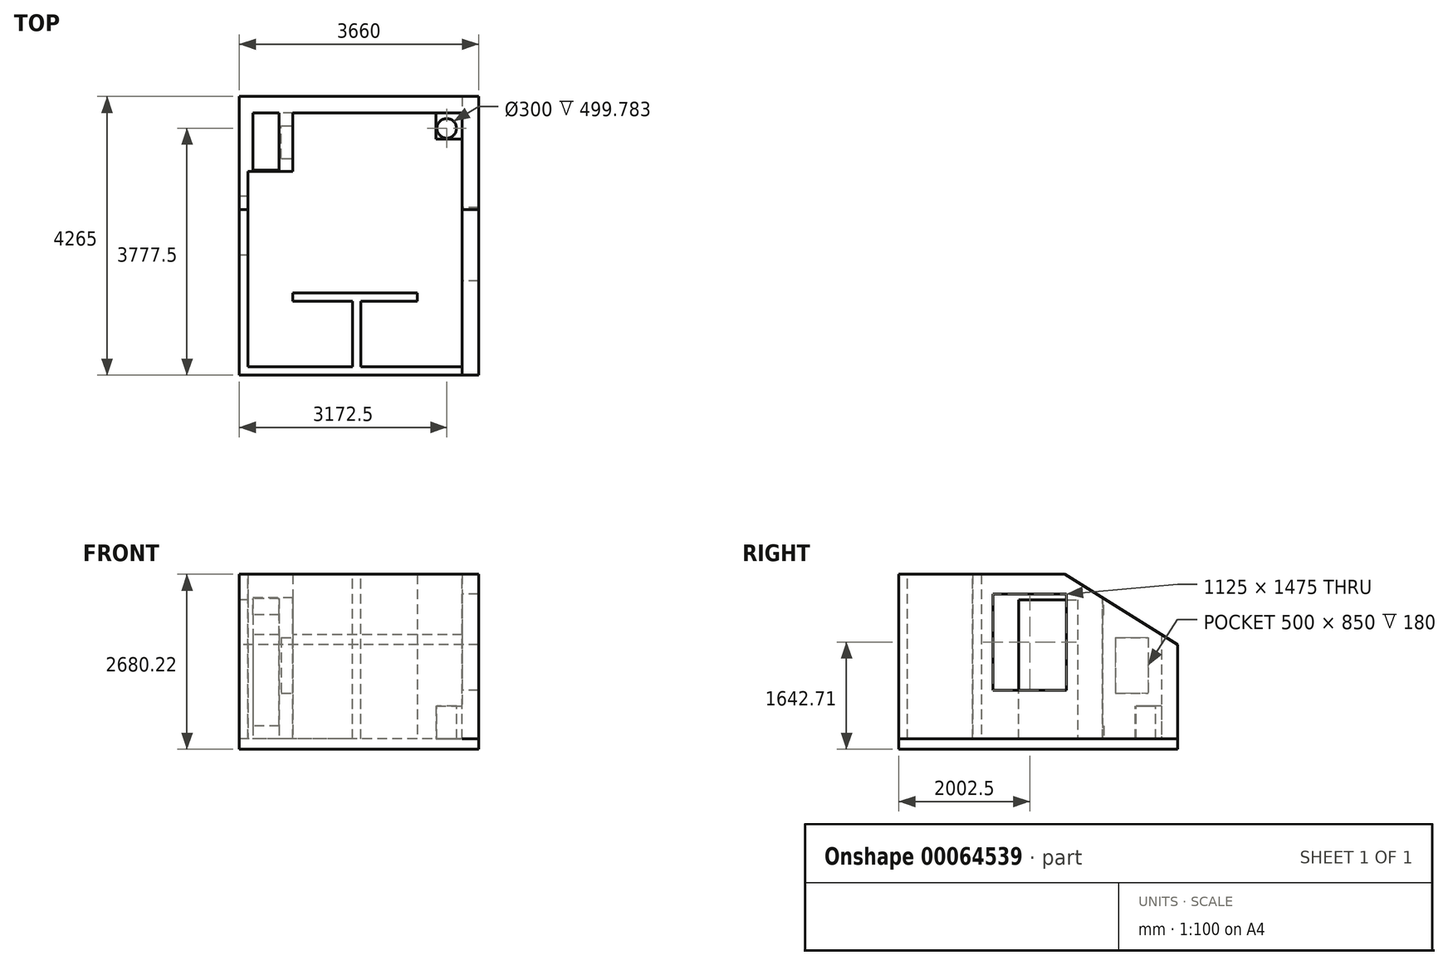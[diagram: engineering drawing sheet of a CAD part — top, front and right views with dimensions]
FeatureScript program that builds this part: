
annotation { "Feature Type Name" : "Feature", "Feature Type Description" : "" }
export const myFeature = defineFeature(function(context is Context, id is Id, definition is map)
    precondition{}
    {
        {
            var Q0;
            Q0=qCreatedBy(makeId("Right.planeOp"),FACE);
            var sketch = newSketch(context, id + "F0", { "sketchPlane" : qUnion([Q0])});
            skLineSegment(sketch, "E0", {"start": v(-1232.64, -1486.91) * mm, "end": v(-1232.64, 1033.09) * mm});
            skLineSegment(sketch, "E1", {"start": v(-1232.64, 1033.09) * mm, "end": v(1304, 1033.09) * mm});
            skLineSegment(sketch, "E2", {"start": v(1304, 1033.09) * mm, "end": v(2782.36, 109.3) * mm});
            skLineSegment(sketch, "E3", {"start": v(2782.36, 109.3) * mm, "end": v(2782.36, -1486.91) * mm});
            skLineSegment(sketch, "E4", {"start": v(2782.36, -1486.91) * mm, "end": v(-1232.64, -1486.91) * mm});
            skLineSegment(sketch, "E5", {"start": v(602.36, -1486.91) * mm, "end": v(602.36, 643.09) * mm});
            skLineSegment(sketch, "E6", {"start": v(602.36, 643.09) * mm, "end": v(1502.36, 643.09) * mm});
            skLineSegment(sketch, "E7", {"start": v(1502.36, 643.09) * mm, "end": v(1502.36, -1486.91) * mm});
            skLineSegment(sketch, "E8", {"start": v(1882.36, 671.69) * mm, "end": v(1882.36, -1486.91) * mm});
            skLineSegment(sketch, "E9", {"start": v(2782.36, -1486.91) * mm, "end": v(3032.36, -1486.91) * mm});
            skLineSegment(sketch, "E10", {"start": v(3032.36, -1486.91) * mm, "end": v(3032.36, -46.91) * mm});
            skLineSegment(sketch, "E11", {"start": v(3032.36, -46.91) * mm, "end": v(2782.36, 109.3) * mm});
            skSolve(sketch);
        }
        {
            var Q0;
            {var subQ6=sQuery(id+"F0.wireOp",EDGE,"E0");Q0=makeQuery(id+"F0.imprint","IMPRINT",FACE,{"disambiguationData":[TD([[makeQuery(id+"F0.imprint","IMPRINT",EDGE,{"derivedFrom":subQ6}),-1.0]])]});}
            extrude(context, id + "F1", {"entities" : qUnion([Q0]), "depth" : 130 * mm});
        }
        {
            var Q0;
            {var subQ0=sQuery(id+"F0.wireOp",EDGE,"E3");Q0=makeQuery(id+"F0.imprint","IMPRINT",FACE,{"disambiguationData":[TD([[makeQuery(id+"F0.imprint","IMPRINT",EDGE,{"derivedFrom":subQ0}),-1.0]])]});}
            extrude(context, id + "F2", {"entities" : qUnion([Q0]), "operationType" : NewBodyOperationType.ADD, "depth" : 210 * mm});
        }
        {
            var Q0;
            Q0=makeQuery(id+"F0.imprint","IMPRINT",FACE,{"disambiguationData":[TD([[makeQuery(id+"F0.imprint","IMPRINT",EDGE,{"derivedFrom":sQuery(id+"F0.wireOp",EDGE,"E3")}),1.0]])]});
            extrude(context, id + "F3", {"entities" : qUnion([Q0]), "operationType" : NewBodyOperationType.ADD, "depth" : 3280 * mm + 130 * mm});
        }
        {
            var Q0;
            Q0=makeQuery(id+"F3.opExtrude","CAP_FACE",FACE,{"disambiguationData":[OSD([sQuery(id+"F0.wireOp",EDGE,"E3"),sQuery(id+"F0.wireOp",EDGE,"E9"),sQuery(id+"F0.wireOp",EDGE,"E10"),sQuery(id+"F0.wireOp",EDGE,"E11")])],"isStart":false});
            var sketch = newSketch(context, id + "F4", { "sketchPlane" : qUnion([Q0])});
            skLineSegment(sketch, "E12", {"start": v(-1232.64, -1486.7) * mm, "end": v(-1232.64, 1033.3) * mm});
            skLineSegment(sketch, "E13", {"start": v(-1232.64, 1033.3) * mm, "end": v(1303.65, 1033.3) * mm});
            skLineSegment(sketch, "E14", {"start": v(1303.65, 1033.3) * mm, "end": v(2782.36, 109.3) * mm});
            skLineSegment(sketch, "E15", {"start": v(2782.36, 109.3) * mm, "end": v(2782.36, -1486.7) * mm});
            skLineSegment(sketch, "E16", {"start": v(2782.36, -1486.7) * mm, "end": v(-1232.64, -1486.7) * mm});
            skLineSegment(sketch, "E17", {"start": v(1882.36, 671.69) * mm, "end": v(1882.36, -1486.7) * mm});
            skLineSegment(sketch, "E18", {"start": v(2782.36, -1486.7) * mm, "end": v(3032.36, -1486.7) * mm});
            skLineSegment(sketch, "E19", {"start": v(3032.36, -1486.7) * mm, "end": v(3032.36, -46.91) * mm});
            skLineSegment(sketch, "E20", {"start": v(3032.36, -46.91) * mm, "end": v(2782.36, 109.3) * mm});
            skLineSegment(sketch, "E21.bottom", {"start": v(207.36, 733.3) * mm, "end": v(1332.36, 733.3) * mm});
            skLineSegment(sketch, "E21.top", {"start": v(207.36, -741.7) * mm, "end": v(1332.36, -741.7) * mm});
            skLineSegment(sketch, "E21.left", {"start": v(207.36, 733.3) * mm, "end": v(207.36, -741.7) * mm});
            skLineSegment(sketch, "E21.right", {"start": v(1332.36, 733.3) * mm, "end": v(1332.36, -741.7) * mm});
            skSolve(sketch);
        }
        {
            var Q0;
            Q0 = qSketchRegion(id + "F4", true);
            extrude(context, id + "F5", {"entities" : qUnion([Q0]), "operationType" : NewBodyOperationType.ADD, "depth" : 250 * mm});
        }
        {
            var Q0;
            Q0=makeQuery(id+"F2.opExtrude","CAP_FACE",FACE,{"disambiguationData":[OSD([sQuery(id+"F0.wireOp",EDGE,"E2"),sQuery(id+"F0.wireOp",EDGE,"E3"),sQuery(id+"F0.wireOp",EDGE,"E4"),sQuery(id+"F0.wireOp",EDGE,"E8")])],"isStart":false});
            cPlane(context, id + "F6", {"entities" : qUnion([Q0]), "cplaneType" : CPlaneType.OFFSET, "offset" : 400 * mm, "width" : 150 * mm, "height" : 150 * mm});
        }
        {
            var Q0;
            Q0=qCreatedBy(id+"F6.planeOp",FACE);
            var sketch = newSketch(context, id + "F7", { "sketchPlane" : qUnion([Q0])});
            skLineSegment(sketch, "E22", {"start": v(1882.36, 671.69) * mm, "end": v(2782.36, 109.3) * mm});
            skLineSegment(sketch, "E23", {"start": v(2782.36, 109.3) * mm, "end": v(2782.36, -1486.7) * mm});
            skLineSegment(sketch, "E24", {"start": v(2782.36, -1486.7) * mm, "end": v(2782.36, -1486.7) * mm});
            skLineSegment(sketch, "E25", {"start": v(2782.36, 109.3) * mm, "end": v(2782.36, 109.3) * mm});
            skLineSegment(sketch, "E26", {"start": v(2782.36, -1486.7) * mm, "end": v(1882.36, -1486.7) * mm});
            skLineSegment(sketch, "E27", {"start": v(1882.36, -1486.7) * mm, "end": v(1882.36, 671.69) * mm});
            skSolve(sketch);
        }
        {
            var Q0;
            Q0 = qSketchRegion(id + "F7", true);
            extrude(context, id + "F8", {"entities" : qUnion([Q0]), "depth" : 210 * mm});
        }
        {
            var Q0;
            Q0=makeQuery(id+"F8.opExtrude","CAP_FACE",FACE,{"disambiguationData":[OSD([sQuery(id+"F7.wireOp",EDGE,"E22"),sQuery(id+"F7.wireOp",EDGE,"E23"),sQuery(id+"F7.wireOp",EDGE,"E26"),sQuery(id+"F7.wireOp",EDGE,"E27")])],"isStart":false});
            var sketch = newSketch(context, id + "F9", { "sketchPlane" : qUnion([Q0])});
            skLineSegment(sketch, "E28.bottom", {"start": v(2082.36, 63.3) * mm, "end": v(2582.36, 63.3) * mm});
            skLineSegment(sketch, "E28.top", {"start": v(2082.36, -786.7) * mm, "end": v(2582.36, -786.7) * mm});
            skLineSegment(sketch, "E28.left", {"start": v(2082.36, 63.3) * mm, "end": v(2082.36, -786.7) * mm});
            skLineSegment(sketch, "E28.right", {"start": v(2582.36, 63.3) * mm, "end": v(2582.36, -786.7) * mm});
            skSolve(sketch);
        }
        {
            var Q0;
            Q0=makeQuery(id+"F9.imprint","IMPRINT",FACE,{"disambiguationData":[TD([[makeQuery(id+"F9.imprint","IMPRINT",EDGE,{"derivedFrom":sQuery(id+"F9.wireOp",EDGE,"E28.bottom")}),-1.0]])]});
            extrude(context, id + "F10", {"entities" : qUnion([Q0]), "operationType" : NewBodyOperationType.REMOVE, "oppositeDirection" : true, "depth" : 180 * mm});
        }
        {
            var Q0;
            Q0=makeQuery(id+"F2.opExtrude","CAP_FACE",FACE,{"disambiguationData":[OSD([sQuery(id+"F0.wireOp",EDGE,"E2"),sQuery(id+"F0.wireOp",EDGE,"E3"),sQuery(id+"F0.wireOp",EDGE,"E4"),sQuery(id+"F0.wireOp",EDGE,"E8")])],"isStart":false});
            var sketch = newSketch(context, id + "F11", { "sketchPlane" : qUnion([Q0])});
            skLineSegment(sketch, "E29", {"start": v(1882.36, 671.69) * mm, "end": v(1882.36, 413.09) * mm});
            skLineSegment(sketch, "E30", {"start": v(1882.36, 413.09) * mm, "end": v(1902.36, 413.09) * mm});
            skLineSegment(sketch, "E31", {"start": v(1902.36, 413.09) * mm, "end": v(1902.36, 659.2) * mm});
            skLineSegment(sketch, "E32", {"start": v(1902.36, 659.2) * mm, "end": v(1882.36, 671.69) * mm});
            skLineSegment(sketch, "E33", {"start": v(1882.36, -1486.91) * mm, "end": v(1882.36, -1286.91) * mm});
            skLineSegment(sketch, "E34", {"start": v(1882.36, -1286.91) * mm, "end": v(1902.36, -1286.91) * mm});
            skLineSegment(sketch, "E35", {"start": v(1902.36, -1286.91) * mm, "end": v(1902.36, -1486.91) * mm});
            skLineSegment(sketch, "E36", {"start": v(1902.36, -1486.91) * mm, "end": v(1882.36, -1486.91) * mm});
            skSolve(sketch);
        }
        {
            var Q0;
            Q0=makeQuery(id+"F11.imprint","IMPRINT",FACE,{"disambiguationData":[TD([[makeQuery(id+"F11.imprint","IMPRINT",EDGE,{"derivedFrom":sQuery(id+"F11.wireOp",EDGE,"E33")}),1.0]])]});
            var Q1;
            Q1=makeQuery(id+"F11.imprint","IMPRINT",FACE,{"disambiguationData":[TD([[makeQuery(id+"F11.imprint","IMPRINT",EDGE,{"derivedFrom":sQuery(id+"F11.wireOp",EDGE,"E29")}),1.0]])]});
            extrude(context, id + "F12", {"entities" : qUnion([Q0, Q1]), "operationType" : NewBodyOperationType.ADD, "depth" : 400 * mm});
        }
        {
            var Q0;
            Q0=makeQuery(id+"F5.opExtrude","CAP_FACE",FACE,{"disambiguationData":[OSD([sQuery(id+"F4.wireOp",EDGE,"E12"),sQuery(id+"F4.wireOp",EDGE,"E13"),sQuery(id+"F4.wireOp",EDGE,"E14"),sQuery(id+"F4.wireOp",EDGE,"E16"),sQuery(id+"F4.wireOp",EDGE,"E18"),sQuery(id+"F4.wireOp",EDGE,"E19"),sQuery(id+"F4.wireOp",EDGE,"E20"),sQuery(id+"F4.wireOp",EDGE,"E21.bottom"),sQuery(id+"F4.wireOp",EDGE,"E21.top"),sQuery(id+"F4.wireOp",EDGE,"E21.left"),sQuery(id+"F4.wireOp",EDGE,"E21.right")])],"isStart":true});
            var sketch = newSketch(context, id + "F13", { "sketchPlane" : qUnion([Q0])});
            skLineSegment(sketch, "E37", {"start": v(-2382.36, -1486.91) * mm, "end": v(-2382.36, 359.25) * mm});
            skLineSegment(sketch, "E38", {"start": v(-2382.36, 359.25) * mm, "end": v(-2257.36, 437.36) * mm});
            skLineSegment(sketch, "E39", {"start": v(-2257.36, 437.36) * mm, "end": v(-2257.36, -1486.91) * mm});
            skLineSegment(sketch, "E40", {"start": v(-2257.36, -1486.91) * mm, "end": v(-2382.36, -1486.91) * mm});
            skLineSegment(sketch, "E41.bottom", {"start": v(-2782.36, -1486.91) * mm, "end": v(-2382.36, -1486.91) * mm});
            skLineSegment(sketch, "E41.top", {"start": v(-2782.36, -986.91) * mm, "end": v(-2382.36, -986.91) * mm});
            skLineSegment(sketch, "E41.left", {"start": v(-2782.36, -1486.91) * mm, "end": v(-2782.36, -986.91) * mm});
            skLineSegment(sketch, "E41.right", {"start": v(-2382.36, -1486.91) * mm, "end": v(-2382.36, -986.91) * mm});
            skSolve(sketch);
        }
        {
            var Q0;
            {var subQ5=sQuery(id+"F13.wireOp",EDGE,"E41.left");Q0=makeQuery(id+"F13.imprint","IMPRINT",FACE,{"disambiguationData":[TD([[makeQuery(id+"F13.imprint","IMPRINT",EDGE,{"derivedFrom":subQ5}),1.0]])]});}
            var Q1;
            {var subQ5=sQuery(id+"F13.wireOp",EDGE,"E41.right");Q1=makeQuery(id+"F13.imprint","IMPRINT",FACE,{"disambiguationData":[TD([[makeQuery(id+"F13.imprint","IMPRINT",EDGE,{"derivedFrom":subQ5}),1.0]])]});}
            extrude(context, id + "F14", {"entities" : qUnion([Q0, Q1]), "operationType" : NewBodyOperationType.ADD, "depth" : 400 * mm});
        }
        {
            var Q0;
            Q0=makeQuery(id+"F14.opExtrude","SWEPT_FACE",FACE,{"disambiguationData":[OSD([sQuery(id+"F13.wireOp",EDGE,"E41.top")])]});
            var sketch = newSketch(context, id + "F15", { "sketchPlane" : qUnion([Q0])});
            skCircle(sketch, "E42", {"center": v(3172.5, 2544.86) * mm, "radius": 150 * mm});
            skSolve(sketch);
        }
        {
            var Q0;
            Q0=makeQuery(id+"F15.imprint","IMPRINT",FACE,{"disambiguationData":[TD([[makeQuery(id+"F15.imprint","IMPRINT",EDGE,{"derivedFrom":sQuery(id+"F15.wireOp",EDGE,"E42")}),1.0]])]});
            var Q1;
            Q1=sQuery(id+"F15.wireOp",EDGE,"E42");
            extrude(context, id + "F16", {"entities" : qUnion([Q0]), "operationType" : NewBodyOperationType.REMOVE, "surfaceEntities" : qUnion([Q1]), "endBound" : BoundingType.UP_TO_NEXT, "oppositeDirection" : true, "depth" : 25 * mm});
        }
        {
            var Q0;
            Q0=makeQuery(id+"F1.opExtrude","CAP_FACE",FACE,{"disambiguationData":[OSD([sQuery(id+"F0.wireOp",EDGE,"E0"),sQuery(id+"F0.wireOp",EDGE,"E1"),sQuery(id+"F0.wireOp",EDGE,"E2"),sQuery(id+"F0.wireOp",EDGE,"E4"),sQuery(id+"F0.wireOp",EDGE,"E5"),sQuery(id+"F0.wireOp",EDGE,"E6"),sQuery(id+"F0.wireOp",EDGE,"E7"),sQuery(id+"F0.wireOp",EDGE,"E8")])],"isStart":false});
            var sketch = newSketch(context, id + "F17", { "sketchPlane" : qUnion([Q0])});
            skLineSegment(sketch, "E43.bottom", {"start": v(-1232.64, -1486.91) * mm, "end": v(-1102.64, -1486.91) * mm});
            skLineSegment(sketch, "E43.top", {"start": v(-1232.64, 1033.09) * mm, "end": v(-1102.64, 1033.09) * mm});
            skLineSegment(sketch, "E43.left", {"start": v(-1232.64, -1486.91) * mm, "end": v(-1232.64, 1033.09) * mm});
            skLineSegment(sketch, "E43.right", {"start": v(-1102.64, -1486.91) * mm, "end": v(-1102.64, 1033.09) * mm});
            skSolve(sketch);
        }
        {
            var Q0;
            Q0=makeQuery(id+"F17.imprint","IMPRINT",FACE,{"disambiguationData":[TD([[makeQuery(id+"F17.imprint","IMPRINT",EDGE,{"derivedFrom":sQuery(id+"F17.wireOp",EDGE,"E43.bottom")}),-1.0]])]});
            var Q1;
            Q1=makeQuery(id+"F5.opExtrude","CAP_FACE",FACE,{"disambiguationData":[OSD([sQuery(id+"F4.wireOp",EDGE,"E12"),sQuery(id+"F4.wireOp",EDGE,"E13"),sQuery(id+"F4.wireOp",EDGE,"E14"),sQuery(id+"F4.wireOp",EDGE,"E16"),sQuery(id+"F4.wireOp",EDGE,"E18"),sQuery(id+"F4.wireOp",EDGE,"E19"),sQuery(id+"F4.wireOp",EDGE,"E20"),sQuery(id+"F4.wireOp",EDGE,"E21.bottom"),sQuery(id+"F4.wireOp",EDGE,"E21.top"),sQuery(id+"F4.wireOp",EDGE,"E21.left"),sQuery(id+"F4.wireOp",EDGE,"E21.right")])],"isStart":true});
            extrude(context, id + "F18", {"entities" : qUnion([Q0]), "operationType" : NewBodyOperationType.ADD, "endBound" : BoundingType.UP_TO_SURFACE, "endBoundEntityFace" : qUnion([Q1]), "depth" : 25 * mm});
        }
        {
            var Q0;
            Q0=makeQuery(id+"F18.opExtrude","SWEPT_FACE",FACE,{"disambiguationData":[OSD([sQuery(id+"F17.wireOp",EDGE,"E43.right")])]});
            var sketch = newSketch(context, id + "F19", { "sketchPlane" : qUnion([Q0])});
            skLineSegment(sketch, "E44.bottom", {"start": v(-1860, -1486.91) * mm, "end": v(-1730, -1486.91) * mm});
            skLineSegment(sketch, "E44.top", {"start": v(-1860, 1033.09) * mm, "end": v(-1730, 1033.09) * mm});
            skLineSegment(sketch, "E44.left", {"start": v(-1860, -1486.91) * mm, "end": v(-1860, 1033.09) * mm});
            skLineSegment(sketch, "E44.right", {"start": v(-1730, -1486.91) * mm, "end": v(-1730, 1033.09) * mm});
            skSolve(sketch);
        }
        {
            var Q0;
            Q0=makeQuery(id+"F19.imprint","IMPRINT",FACE,{"disambiguationData":[TD([[makeQuery(id+"F19.imprint","IMPRINT",EDGE,{"derivedFrom":sQuery(id+"F19.wireOp",EDGE,"E44.bottom")}),1.0]])]});
            extrude(context, id + "F20", {"entities" : qUnion([Q0]), "operationType" : NewBodyOperationType.ADD, "depth" : 1000 * mm});
        }
        {
            var Q0;
            Q0=makeQuery(id+"F20.opExtrude","CAP_FACE",FACE,{"disambiguationData":[OSD([sQuery(id+"F19.wireOp",EDGE,"E44.bottom"),sQuery(id+"F19.wireOp",EDGE,"E44.top"),sQuery(id+"F19.wireOp",EDGE,"E44.left"),sQuery(id+"F19.wireOp",EDGE,"E44.right")])],"isStart":false});
            var sketch = newSketch(context, id + "F21", { "sketchPlane" : qUnion([Q0])});
            skLineSegment(sketch, "E45.bottom", {"start": v(-2720, 1033.09) * mm, "end": v(-820, 1033.09) * mm});
            skLineSegment(sketch, "E45.top", {"start": v(-2720, -1486.91) * mm, "end": v(-820, -1486.91) * mm});
            skLineSegment(sketch, "E45.left", {"start": v(-2720, 1033.09) * mm, "end": v(-2720, -1486.91) * mm});
            skLineSegment(sketch, "E45.right", {"start": v(-820, 1033.09) * mm, "end": v(-820, -1486.91) * mm});
            skSolve(sketch);
        }
        {
            var Q0;
            {var subQ2=sQuery(id+"F21.wireOp",EDGE,"E45.left");Q0=makeQuery(id+"F21.imprint","IMPRINT",FACE,{"disambiguationData":[TD([[makeQuery(id+"F21.imprint","IMPRINT",EDGE,{"derivedFrom":subQ2}),1.0]])]});}
            var Q1;
            {var subQ1=makeQuery(id+"F20.opExtrude","CAP_EDGE",EDGE,{"disambiguationData":[OSD([sQuery(id+"F19.wireOp",EDGE,"E44.left")])],"isStart":false});Q1=makeQuery(id+"F21.imprint","IMPRINT",FACE,{"disambiguationData":[TD([[makeQuery(id+"F21.imprint","IMPRINT",EDGE,{"derivedFrom":subQ1}),-1.0]])]});}
            var Q2;
            {var subQ2=sQuery(id+"F21.wireOp",EDGE,"E45.right");Q2=makeQuery(id+"F21.imprint","IMPRINT",FACE,{"disambiguationData":[TD([[makeQuery(id+"F21.imprint","IMPRINT",EDGE,{"derivedFrom":subQ2}),-1.0]])]});}
            extrude(context, id + "F22", {"entities" : qUnion([Q0, Q1, Q2]), "operationType" : NewBodyOperationType.ADD, "depth" : 130 * mm});
        }
        {
            var Q0;
            {var subQ0=sQuery(id+"F0.wireOp",EDGE,"E4");Q0=makeQuery(id+"F22.boolean.opBoolean","MERGE",FACE,{"derivedFrom":[makeQuery(id+"F20.boolean.opBoolean","MERGE",FACE,{"derivedFrom":[makeQuery(id+"F18.boolean.opBoolean","MERGE",FACE,{"derivedFrom":[makeQuery(id+"F1.opExtrude","SWEPT_FACE",FACE,{"disambiguationData":[OSD([subQ0]),TDD([makeQuery(id+"F0.imprint","IMPRINT",EDGE,{"disambiguationData":[TD([[makeQuery(id+"F0.imprint","INTERSECT",VERTEX,{"derivedFrom":[sQuery(id+"F0.wireOp",EDGE,"E0"),subQ0]}),1.0]])],"derivedFrom":subQ0})])]}),makeQuery(id+"F18.opExtrude","SWEPT_FACE",FACE,{"disambiguationData":[OSD([sQuery(id+"F17.wireOp",EDGE,"E43.bottom")])]})]}),makeQuery(id+"F20.opExtrude","SWEPT_FACE",FACE,{"disambiguationData":[OSD([sQuery(id+"F19.wireOp",EDGE,"E44.bottom")])]})]}),makeQuery(id+"F22.opExtrude","SWEPT_FACE",FACE,{"disambiguationData":[OSD([sQuery(id+"F21.wireOp",EDGE,"E45.top")])]})]});}
            var sketch = newSketch(context, id + "F23", { "sketchPlane" : qUnion([Q0])});
            skLineSegment(sketch, "E46.bottom", {"start": v(0, 1232.64) * mm, "end": v(3660, 1232.64) * mm});
            skLineSegment(sketch, "E46.top", {"start": v(0, -3032.36) * mm, "end": v(3660, -3032.36) * mm});
            skLineSegment(sketch, "E46.left", {"start": v(0, 1232.64) * mm, "end": v(0, -3032.36) * mm});
            skLineSegment(sketch, "E46.right", {"start": v(3660, 1232.64) * mm, "end": v(3660, -3032.36) * mm});
            skSolve(sketch);
        }
        {
            var Q0;
            {var subQ15=sQuery(id+"F23.wireOp",EDGE,"E46.top");Q0=makeQuery(id+"F23.imprint","IMPRINT",FACE,{"disambiguationData":[TD([[makeQuery(id+"F23.imprint","IMPRINT",EDGE,{"derivedFrom":subQ15}),1.0]])]});}
            var Q1;
            {var subQ11=sQuery(id+"F17.wireOp",EDGE,"E43.bottom");var subQ21=makeQuery(id+"F18.opExtrude","CAP_EDGE",EDGE,{"disambiguationData":[OSD([subQ11])],"isStart":false});Q1=makeQuery(id+"F23.imprint","IMPRINT",FACE,{"disambiguationData":[TD([[makeQuery(id+"F23.imprint","IMPRINT",EDGE,{"derivedFrom":subQ21}),1.0]])]});}
            extrude(context, id + "F24", {"entities" : qUnion([Q0, Q1]), "operationType" : NewBodyOperationType.ADD, "depth" : 160 * mm});
        }
    });
